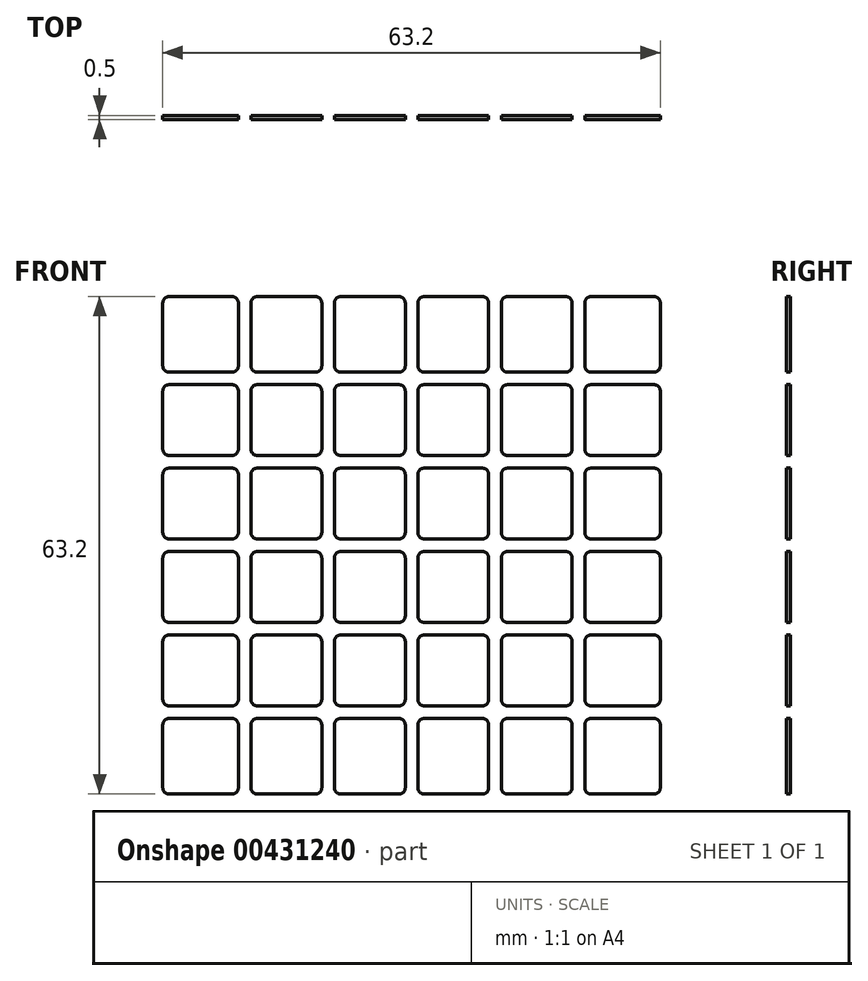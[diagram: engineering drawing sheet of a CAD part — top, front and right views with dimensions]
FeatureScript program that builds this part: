
annotation { "Feature Type Name" : "Feature", "Feature Type Description" : "" }
export const myFeature = defineFeature(function(context is Context, id is Id, definition is map)
    precondition{}
    {
        {
            var Q0;
            Q0=qCreatedBy(makeId("Front.planeOp"),FACE);
            var sketch = newSketch(context, id + "F0", { "sketchPlane" : qUnion([Q0])});
            skLineSegment(sketch, "E0.bottom", {"start": v(0.8, 0) * mm, "end": v(8.2, 0) * mm});
            skLineSegment(sketch, "E0.top", {"start": v(0.8, 9) * mm, "end": v(8.2, 9) * mm});
            skLineSegment(sketch, "E0.left", {"start": v(0, 0.8) * mm, "end": v(0, 8.2) * mm});
            skLineSegment(sketch, "E0.right", {"start": v(9, 0.8) * mm, "end": v(9, 8.2) * mm});
            skPoint(sketch, "E1.visualSharp", {"position": v(0, 9) * mm});
            skArc(sketch, "E1.filletArc", {"start": v(0.8, 9) * mm, "mid": v(0.23, 8.77) * mm, "end": v(0, 8.2) * mm});
            skPoint(sketch, "E2.visualSharp", {"position": v(9, 9) * mm});
            skArc(sketch, "E2.filletArc", {"start": v(9, 8.2) * mm, "mid": v(8.77, 8.77) * mm, "end": v(8.2, 9) * mm});
            skPoint(sketch, "E3.visualSharp", {"position": v(9, 0) * mm});
            skArc(sketch, "E3.filletArc", {"start": v(8.2, 0) * mm, "mid": v(8.77, 0.23) * mm, "end": v(9, 0.8) * mm});
            skPoint(sketch, "E4.visualSharp", {"position": v(0, 0) * mm});
            skArc(sketch, "E4.filletArc", {"start": v(0, 0.8) * mm, "mid": v(0.23, 0.23) * mm, "end": v(0.8, 0) * mm});
            skLineSegment(sketch, "E5.0.1.0", {"start": v(9, 11.4) * mm, "end": v(9, 18.8) * mm});
            skPoint(sketch, "E5.0.1.1", {"position": v(0, 10.6) * mm});
            skLineSegment(sketch, "E5.0.1.2", {"start": v(0, 11.4) * mm, "end": v(0, 18.8) * mm});
            skLineSegment(sketch, "E5.0.1.3", {"start": v(0.8, 10.6) * mm, "end": v(8.2, 10.6) * mm});
            skPoint(sketch, "E5.0.1.4", {"position": v(9, 10.6) * mm});
            skLineSegment(sketch, "E5.0.1.5", {"start": v(0.8, 19.6) * mm, "end": v(8.2, 19.6) * mm});
            skPoint(sketch, "E5.0.1.6", {"position": v(0, 19.6) * mm});
            skPoint(sketch, "E5.0.1.7", {"position": v(9, 19.6) * mm});
            skArc(sketch, "E5.0.1.8", {"start": v(8.2, 10.6) * mm, "mid": v(8.77, 10.83) * mm, "end": v(9, 11.4) * mm});
            skArc(sketch, "E5.0.1.9", {"start": v(0.8, 19.6) * mm, "mid": v(0.23, 19.37) * mm, "end": v(0, 18.8) * mm});
            skArc(sketch, "E5.0.1.10", {"start": v(0, 11.4) * mm, "mid": v(0.23, 10.83) * mm, "end": v(0.8, 10.6) * mm});
            skArc(sketch, "E5.0.1.11", {"start": v(9, 18.8) * mm, "mid": v(8.77, 19.37) * mm, "end": v(8.2, 19.6) * mm});
            skLineSegment(sketch, "E5.0.2.0", {"start": v(9, 22) * mm, "end": v(9, 29.4) * mm});
            skPoint(sketch, "E5.0.2.1", {"position": v(0, 21.2) * mm});
            skLineSegment(sketch, "E5.0.2.2", {"start": v(0, 22) * mm, "end": v(0, 29.4) * mm});
            skLineSegment(sketch, "E5.0.2.3", {"start": v(0.8, 21.2) * mm, "end": v(8.2, 21.2) * mm});
            skPoint(sketch, "E5.0.2.4", {"position": v(9, 21.2) * mm});
            skLineSegment(sketch, "E5.0.2.5", {"start": v(0.8, 30.2) * mm, "end": v(8.2, 30.2) * mm});
            skPoint(sketch, "E5.0.2.6", {"position": v(0, 30.2) * mm});
            skPoint(sketch, "E5.0.2.7", {"position": v(9, 30.2) * mm});
            skArc(sketch, "E5.0.2.8", {"start": v(8.2, 21.2) * mm, "mid": v(8.77, 21.43) * mm, "end": v(9, 22) * mm});
            skArc(sketch, "E5.0.2.9", {"start": v(0.8, 30.2) * mm, "mid": v(0.23, 29.97) * mm, "end": v(0, 29.4) * mm});
            skArc(sketch, "E5.0.2.10", {"start": v(0, 22) * mm, "mid": v(0.23, 21.43) * mm, "end": v(0.8, 21.2) * mm});
            skArc(sketch, "E5.0.2.11", {"start": v(9, 29.4) * mm, "mid": v(8.77, 29.97) * mm, "end": v(8.2, 30.2) * mm});
            skLineSegment(sketch, "E5.0.3.0", {"start": v(9, 32.6) * mm, "end": v(9, 40) * mm});
            skPoint(sketch, "E5.0.3.1", {"position": v(0, 31.8) * mm});
            skLineSegment(sketch, "E5.0.3.2", {"start": v(0, 32.6) * mm, "end": v(0, 40) * mm});
            skLineSegment(sketch, "E5.0.3.3", {"start": v(0.8, 31.8) * mm, "end": v(8.2, 31.8) * mm});
            skPoint(sketch, "E5.0.3.4", {"position": v(9, 31.8) * mm});
            skLineSegment(sketch, "E5.0.3.5", {"start": v(0.8, 40.8) * mm, "end": v(8.2, 40.8) * mm});
            skPoint(sketch, "E5.0.3.6", {"position": v(0, 40.8) * mm});
            skPoint(sketch, "E5.0.3.7", {"position": v(9, 40.8) * mm});
            skArc(sketch, "E5.0.3.8", {"start": v(8.2, 31.8) * mm, "mid": v(8.77, 32.03) * mm, "end": v(9, 32.6) * mm});
            skArc(sketch, "E5.0.3.9", {"start": v(0.8, 40.8) * mm, "mid": v(0.23, 40.57) * mm, "end": v(0, 40) * mm});
            skArc(sketch, "E5.0.3.10", {"start": v(0, 32.6) * mm, "mid": v(0.23, 32.03) * mm, "end": v(0.8, 31.8) * mm});
            skArc(sketch, "E5.0.3.11", {"start": v(9, 40) * mm, "mid": v(8.77, 40.57) * mm, "end": v(8.2, 40.8) * mm});
            skLineSegment(sketch, "E5.1.0.0", {"start": v(19.6, 0.8) * mm, "end": v(19.6, 8.2) * mm});
            skPoint(sketch, "E5.1.0.1", {"position": v(10.6, 0) * mm});
            skLineSegment(sketch, "E5.1.0.2", {"start": v(10.6, 0.8) * mm, "end": v(10.6, 8.2) * mm});
            skLineSegment(sketch, "E5.1.0.3", {"start": v(11.4, 0) * mm, "end": v(18.8, 0) * mm});
            skPoint(sketch, "E5.1.0.4", {"position": v(19.6, 0) * mm});
            skLineSegment(sketch, "E5.1.0.5", {"start": v(11.4, 9) * mm, "end": v(18.8, 9) * mm});
            skPoint(sketch, "E5.1.0.6", {"position": v(10.6, 9) * mm});
            skPoint(sketch, "E5.1.0.7", {"position": v(19.6, 9) * mm});
            skArc(sketch, "E5.1.0.8", {"start": v(18.8, 0) * mm, "mid": v(19.37, 0.23) * mm, "end": v(19.6, 0.8) * mm});
            skArc(sketch, "E5.1.0.9", {"start": v(11.4, 9) * mm, "mid": v(10.83, 8.77) * mm, "end": v(10.6, 8.2) * mm});
            skArc(sketch, "E5.1.0.10", {"start": v(10.6, 0.8) * mm, "mid": v(10.83, 0.23) * mm, "end": v(11.4, 0) * mm});
            skArc(sketch, "E5.1.0.11", {"start": v(19.6, 8.2) * mm, "mid": v(19.37, 8.77) * mm, "end": v(18.8, 9) * mm});
            skLineSegment(sketch, "E5.1.1.0", {"start": v(19.6, 11.4) * mm, "end": v(19.6, 18.8) * mm});
            skPoint(sketch, "E5.1.1.1", {"position": v(10.6, 10.6) * mm});
            skLineSegment(sketch, "E5.1.1.2", {"start": v(10.6, 11.4) * mm, "end": v(10.6, 18.8) * mm});
            skLineSegment(sketch, "E5.1.1.3", {"start": v(11.4, 10.6) * mm, "end": v(18.8, 10.6) * mm});
            skPoint(sketch, "E5.1.1.4", {"position": v(19.6, 10.6) * mm});
            skLineSegment(sketch, "E5.1.1.5", {"start": v(11.4, 19.6) * mm, "end": v(18.8, 19.6) * mm});
            skPoint(sketch, "E5.1.1.6", {"position": v(10.6, 19.6) * mm});
            skPoint(sketch, "E5.1.1.7", {"position": v(19.6, 19.6) * mm});
            skArc(sketch, "E5.1.1.8", {"start": v(18.8, 10.6) * mm, "mid": v(19.37, 10.83) * mm, "end": v(19.6, 11.4) * mm});
            skArc(sketch, "E5.1.1.9", {"start": v(11.4, 19.6) * mm, "mid": v(10.83, 19.37) * mm, "end": v(10.6, 18.8) * mm});
            skArc(sketch, "E5.1.1.10", {"start": v(10.6, 11.4) * mm, "mid": v(10.83, 10.83) * mm, "end": v(11.4, 10.6) * mm});
            skArc(sketch, "E5.1.1.11", {"start": v(19.6, 18.8) * mm, "mid": v(19.37, 19.37) * mm, "end": v(18.8, 19.6) * mm});
            skLineSegment(sketch, "E5.1.2.0", {"start": v(19.6, 22) * mm, "end": v(19.6, 29.4) * mm});
            skPoint(sketch, "E5.1.2.1", {"position": v(10.6, 21.2) * mm});
            skLineSegment(sketch, "E5.1.2.2", {"start": v(10.6, 22) * mm, "end": v(10.6, 29.4) * mm});
            skLineSegment(sketch, "E5.1.2.3", {"start": v(11.4, 21.2) * mm, "end": v(18.8, 21.2) * mm});
            skPoint(sketch, "E5.1.2.4", {"position": v(19.6, 21.2) * mm});
            skLineSegment(sketch, "E5.1.2.5", {"start": v(11.4, 30.2) * mm, "end": v(18.8, 30.2) * mm});
            skPoint(sketch, "E5.1.2.6", {"position": v(10.6, 30.2) * mm});
            skPoint(sketch, "E5.1.2.7", {"position": v(19.6, 30.2) * mm});
            skArc(sketch, "E5.1.2.8", {"start": v(18.8, 21.2) * mm, "mid": v(19.37, 21.43) * mm, "end": v(19.6, 22) * mm});
            skArc(sketch, "E5.1.2.9", {"start": v(11.4, 30.2) * mm, "mid": v(10.83, 29.97) * mm, "end": v(10.6, 29.4) * mm});
            skArc(sketch, "E5.1.2.10", {"start": v(10.6, 22) * mm, "mid": v(10.83, 21.43) * mm, "end": v(11.4, 21.2) * mm});
            skArc(sketch, "E5.1.2.11", {"start": v(19.6, 29.4) * mm, "mid": v(19.37, 29.97) * mm, "end": v(18.8, 30.2) * mm});
            skLineSegment(sketch, "E5.1.3.0", {"start": v(19.6, 32.6) * mm, "end": v(19.6, 40) * mm});
            skPoint(sketch, "E5.1.3.1", {"position": v(10.6, 31.8) * mm});
            skLineSegment(sketch, "E5.1.3.2", {"start": v(10.6, 32.6) * mm, "end": v(10.6, 40) * mm});
            skLineSegment(sketch, "E5.1.3.3", {"start": v(11.4, 31.8) * mm, "end": v(18.8, 31.8) * mm});
            skPoint(sketch, "E5.1.3.4", {"position": v(19.6, 31.8) * mm});
            skLineSegment(sketch, "E5.1.3.5", {"start": v(11.4, 40.8) * mm, "end": v(18.8, 40.8) * mm});
            skPoint(sketch, "E5.1.3.6", {"position": v(10.6, 40.8) * mm});
            skPoint(sketch, "E5.1.3.7", {"position": v(19.6, 40.8) * mm});
            skArc(sketch, "E5.1.3.8", {"start": v(18.8, 31.8) * mm, "mid": v(19.37, 32.03) * mm, "end": v(19.6, 32.6) * mm});
            skArc(sketch, "E5.1.3.9", {"start": v(11.4, 40.8) * mm, "mid": v(10.83, 40.57) * mm, "end": v(10.6, 40) * mm});
            skArc(sketch, "E5.1.3.10", {"start": v(10.6, 32.6) * mm, "mid": v(10.83, 32.03) * mm, "end": v(11.4, 31.8) * mm});
            skArc(sketch, "E5.1.3.11", {"start": v(19.6, 40) * mm, "mid": v(19.37, 40.57) * mm, "end": v(18.8, 40.8) * mm});
            skLineSegment(sketch, "E5.2.0.0", {"start": v(30.2, 0.8) * mm, "end": v(30.2, 8.2) * mm});
            skPoint(sketch, "E5.2.0.1", {"position": v(21.2, 0) * mm});
            skLineSegment(sketch, "E5.2.0.2", {"start": v(21.2, 0.8) * mm, "end": v(21.2, 8.2) * mm});
            skLineSegment(sketch, "E5.2.0.3", {"start": v(22, 0) * mm, "end": v(29.4, 0) * mm});
            skPoint(sketch, "E5.2.0.4", {"position": v(30.2, 0) * mm});
            skLineSegment(sketch, "E5.2.0.5", {"start": v(22, 9) * mm, "end": v(29.4, 9) * mm});
            skPoint(sketch, "E5.2.0.6", {"position": v(21.2, 9) * mm});
            skPoint(sketch, "E5.2.0.7", {"position": v(30.2, 9) * mm});
            skArc(sketch, "E5.2.0.8", {"start": v(29.4, 0) * mm, "mid": v(29.97, 0.23) * mm, "end": v(30.2, 0.8) * mm});
            skArc(sketch, "E5.2.0.9", {"start": v(22, 9) * mm, "mid": v(21.43, 8.77) * mm, "end": v(21.2, 8.2) * mm});
            skArc(sketch, "E5.2.0.10", {"start": v(21.2, 0.8) * mm, "mid": v(21.43, 0.23) * mm, "end": v(22, 0) * mm});
            skArc(sketch, "E5.2.0.11", {"start": v(30.2, 8.2) * mm, "mid": v(29.97, 8.77) * mm, "end": v(29.4, 9) * mm});
            skLineSegment(sketch, "E5.2.1.0", {"start": v(30.2, 11.4) * mm, "end": v(30.2, 18.8) * mm});
            skPoint(sketch, "E5.2.1.1", {"position": v(21.2, 10.6) * mm});
            skLineSegment(sketch, "E5.2.1.2", {"start": v(21.2, 11.4) * mm, "end": v(21.2, 18.8) * mm});
            skLineSegment(sketch, "E5.2.1.3", {"start": v(22, 10.6) * mm, "end": v(29.4, 10.6) * mm});
            skPoint(sketch, "E5.2.1.4", {"position": v(30.2, 10.6) * mm});
            skLineSegment(sketch, "E5.2.1.5", {"start": v(22, 19.6) * mm, "end": v(29.4, 19.6) * mm});
            skPoint(sketch, "E5.2.1.6", {"position": v(21.2, 19.6) * mm});
            skPoint(sketch, "E5.2.1.7", {"position": v(30.2, 19.6) * mm});
            skArc(sketch, "E5.2.1.8", {"start": v(29.4, 10.6) * mm, "mid": v(29.97, 10.83) * mm, "end": v(30.2, 11.4) * mm});
            skArc(sketch, "E5.2.1.9", {"start": v(22, 19.6) * mm, "mid": v(21.43, 19.37) * mm, "end": v(21.2, 18.8) * mm});
            skArc(sketch, "E5.2.1.10", {"start": v(21.2, 11.4) * mm, "mid": v(21.43, 10.83) * mm, "end": v(22, 10.6) * mm});
            skArc(sketch, "E5.2.1.11", {"start": v(30.2, 18.8) * mm, "mid": v(29.97, 19.37) * mm, "end": v(29.4, 19.6) * mm});
            skLineSegment(sketch, "E5.2.2.0", {"start": v(30.2, 22) * mm, "end": v(30.2, 29.4) * mm});
            skPoint(sketch, "E5.2.2.1", {"position": v(21.2, 21.2) * mm});
            skLineSegment(sketch, "E5.2.2.2", {"start": v(21.2, 22) * mm, "end": v(21.2, 29.4) * mm});
            skLineSegment(sketch, "E5.2.2.3", {"start": v(22, 21.2) * mm, "end": v(29.4, 21.2) * mm});
            skPoint(sketch, "E5.2.2.4", {"position": v(30.2, 21.2) * mm});
            skLineSegment(sketch, "E5.2.2.5", {"start": v(22, 30.2) * mm, "end": v(29.4, 30.2) * mm});
            skPoint(sketch, "E5.2.2.6", {"position": v(21.2, 30.2) * mm});
            skPoint(sketch, "E5.2.2.7", {"position": v(30.2, 30.2) * mm});
            skArc(sketch, "E5.2.2.8", {"start": v(29.4, 21.2) * mm, "mid": v(29.97, 21.43) * mm, "end": v(30.2, 22) * mm});
            skArc(sketch, "E5.2.2.9", {"start": v(22, 30.2) * mm, "mid": v(21.43, 29.97) * mm, "end": v(21.2, 29.4) * mm});
            skArc(sketch, "E5.2.2.10", {"start": v(21.2, 22) * mm, "mid": v(21.43, 21.43) * mm, "end": v(22, 21.2) * mm});
            skArc(sketch, "E5.2.2.11", {"start": v(30.2, 29.4) * mm, "mid": v(29.97, 29.97) * mm, "end": v(29.4, 30.2) * mm});
            skLineSegment(sketch, "E5.2.3.0", {"start": v(30.2, 32.6) * mm, "end": v(30.2, 40) * mm});
            skPoint(sketch, "E5.2.3.1", {"position": v(21.2, 31.8) * mm});
            skLineSegment(sketch, "E5.2.3.2", {"start": v(21.2, 32.6) * mm, "end": v(21.2, 40) * mm});
            skLineSegment(sketch, "E5.2.3.3", {"start": v(22, 31.8) * mm, "end": v(29.4, 31.8) * mm});
            skPoint(sketch, "E5.2.3.4", {"position": v(30.2, 31.8) * mm});
            skLineSegment(sketch, "E5.2.3.5", {"start": v(22, 40.8) * mm, "end": v(29.4, 40.8) * mm});
            skPoint(sketch, "E5.2.3.6", {"position": v(21.2, 40.8) * mm});
            skPoint(sketch, "E5.2.3.7", {"position": v(30.2, 40.8) * mm});
            skArc(sketch, "E5.2.3.8", {"start": v(29.4, 31.8) * mm, "mid": v(29.97, 32.03) * mm, "end": v(30.2, 32.6) * mm});
            skArc(sketch, "E5.2.3.9", {"start": v(22, 40.8) * mm, "mid": v(21.43, 40.57) * mm, "end": v(21.2, 40) * mm});
            skArc(sketch, "E5.2.3.10", {"start": v(21.2, 32.6) * mm, "mid": v(21.43, 32.03) * mm, "end": v(22, 31.8) * mm});
            skArc(sketch, "E5.2.3.11", {"start": v(30.2, 40) * mm, "mid": v(29.97, 40.57) * mm, "end": v(29.4, 40.8) * mm});
            skLineSegment(sketch, "E5.3.0.0", {"start": v(40.8, 0.8) * mm, "end": v(40.8, 8.2) * mm});
            skPoint(sketch, "E5.3.0.1", {"position": v(31.8, 0) * mm});
            skLineSegment(sketch, "E5.3.0.2", {"start": v(31.8, 0.8) * mm, "end": v(31.8, 8.2) * mm});
            skLineSegment(sketch, "E5.3.0.3", {"start": v(32.6, 0) * mm, "end": v(40, 0) * mm});
            skPoint(sketch, "E5.3.0.4", {"position": v(40.8, 0) * mm});
            skLineSegment(sketch, "E5.3.0.5", {"start": v(32.6, 9) * mm, "end": v(40, 9) * mm});
            skPoint(sketch, "E5.3.0.6", {"position": v(31.8, 9) * mm});
            skPoint(sketch, "E5.3.0.7", {"position": v(40.8, 9) * mm});
            skArc(sketch, "E5.3.0.8", {"start": v(40, 0) * mm, "mid": v(40.57, 0.23) * mm, "end": v(40.8, 0.8) * mm});
            skArc(sketch, "E5.3.0.9", {"start": v(32.6, 9) * mm, "mid": v(32.03, 8.77) * mm, "end": v(31.8, 8.2) * mm});
            skArc(sketch, "E5.3.0.10", {"start": v(31.8, 0.8) * mm, "mid": v(32.03, 0.23) * mm, "end": v(32.6, 0) * mm});
            skArc(sketch, "E5.3.0.11", {"start": v(40.8, 8.2) * mm, "mid": v(40.57, 8.77) * mm, "end": v(40, 9) * mm});
            skLineSegment(sketch, "E5.3.1.0", {"start": v(40.8, 11.4) * mm, "end": v(40.8, 18.8) * mm});
            skPoint(sketch, "E5.3.1.1", {"position": v(31.8, 10.6) * mm});
            skLineSegment(sketch, "E5.3.1.2", {"start": v(31.8, 11.4) * mm, "end": v(31.8, 18.8) * mm});
            skLineSegment(sketch, "E5.3.1.3", {"start": v(32.6, 10.6) * mm, "end": v(40, 10.6) * mm});
            skPoint(sketch, "E5.3.1.4", {"position": v(40.8, 10.6) * mm});
            skLineSegment(sketch, "E5.3.1.5", {"start": v(32.6, 19.6) * mm, "end": v(40, 19.6) * mm});
            skPoint(sketch, "E5.3.1.6", {"position": v(31.8, 19.6) * mm});
            skPoint(sketch, "E5.3.1.7", {"position": v(40.8, 19.6) * mm});
            skArc(sketch, "E5.3.1.8", {"start": v(40, 10.6) * mm, "mid": v(40.57, 10.83) * mm, "end": v(40.8, 11.4) * mm});
            skArc(sketch, "E5.3.1.9", {"start": v(32.6, 19.6) * mm, "mid": v(32.03, 19.37) * mm, "end": v(31.8, 18.8) * mm});
            skArc(sketch, "E5.3.1.10", {"start": v(31.8, 11.4) * mm, "mid": v(32.03, 10.83) * mm, "end": v(32.6, 10.6) * mm});
            skArc(sketch, "E5.3.1.11", {"start": v(40.8, 18.8) * mm, "mid": v(40.57, 19.37) * mm, "end": v(40, 19.6) * mm});
            skLineSegment(sketch, "E5.3.2.0", {"start": v(40.8, 22) * mm, "end": v(40.8, 29.4) * mm});
            skPoint(sketch, "E5.3.2.1", {"position": v(31.8, 21.2) * mm});
            skLineSegment(sketch, "E5.3.2.2", {"start": v(31.8, 22) * mm, "end": v(31.8, 29.4) * mm});
            skLineSegment(sketch, "E5.3.2.3", {"start": v(32.6, 21.2) * mm, "end": v(40, 21.2) * mm});
            skPoint(sketch, "E5.3.2.4", {"position": v(40.8, 21.2) * mm});
            skLineSegment(sketch, "E5.3.2.5", {"start": v(32.6, 30.2) * mm, "end": v(40, 30.2) * mm});
            skPoint(sketch, "E5.3.2.6", {"position": v(31.8, 30.2) * mm});
            skPoint(sketch, "E5.3.2.7", {"position": v(40.8, 30.2) * mm});
            skArc(sketch, "E5.3.2.8", {"start": v(40, 21.2) * mm, "mid": v(40.57, 21.43) * mm, "end": v(40.8, 22) * mm});
            skArc(sketch, "E5.3.2.9", {"start": v(32.6, 30.2) * mm, "mid": v(32.03, 29.97) * mm, "end": v(31.8, 29.4) * mm});
            skArc(sketch, "E5.3.2.10", {"start": v(31.8, 22) * mm, "mid": v(32.03, 21.43) * mm, "end": v(32.6, 21.2) * mm});
            skArc(sketch, "E5.3.2.11", {"start": v(40.8, 29.4) * mm, "mid": v(40.57, 29.97) * mm, "end": v(40, 30.2) * mm});
            skLineSegment(sketch, "E5.3.3.0", {"start": v(40.8, 32.6) * mm, "end": v(40.8, 40) * mm});
            skPoint(sketch, "E5.3.3.1", {"position": v(31.8, 31.8) * mm});
            skLineSegment(sketch, "E5.3.3.2", {"start": v(31.8, 32.6) * mm, "end": v(31.8, 40) * mm});
            skLineSegment(sketch, "E5.3.3.3", {"start": v(32.6, 31.8) * mm, "end": v(40, 31.8) * mm});
            skPoint(sketch, "E5.3.3.4", {"position": v(40.8, 31.8) * mm});
            skLineSegment(sketch, "E5.3.3.5", {"start": v(32.6, 40.8) * mm, "end": v(40, 40.8) * mm});
            skPoint(sketch, "E5.3.3.6", {"position": v(31.8, 40.8) * mm});
            skPoint(sketch, "E5.3.3.7", {"position": v(40.8, 40.8) * mm});
            skArc(sketch, "E5.3.3.8", {"start": v(40, 31.8) * mm, "mid": v(40.57, 32.03) * mm, "end": v(40.8, 32.6) * mm});
            skArc(sketch, "E5.3.3.9", {"start": v(32.6, 40.8) * mm, "mid": v(32.03, 40.57) * mm, "end": v(31.8, 40) * mm});
            skArc(sketch, "E5.3.3.10", {"start": v(31.8, 32.6) * mm, "mid": v(32.03, 32.03) * mm, "end": v(32.6, 31.8) * mm});
            skArc(sketch, "E5.3.3.11", {"start": v(40.8, 40) * mm, "mid": v(40.57, 40.57) * mm, "end": v(40, 40.8) * mm});
            skLineSegment(sketch, "E5.direction1", {"start": v(0, 0) * mm, "end": v(10.6, 0) * mm, "construction": true});
            skLineSegment(sketch, "E5.direction2", {"start": v(0, 0) * mm, "end": v(0, 10.6) * mm, "construction": true});
            skLineSegment(sketch, "E6.bottom", {"start": v(-2.4, 0) * mm, "end": v(-10.4, 0) * mm});
            skLineSegment(sketch, "E6.top", {"start": v(-2.4, 9) * mm, "end": v(-10.4, 9) * mm});
            skLineSegment(sketch, "E6.left", {"start": v(-1.6, 0.8) * mm, "end": v(-1.6, 8.2) * mm});
            skLineSegment(sketch, "E6.right", {"start": v(-11.2, 0.8) * mm, "end": v(-11.2, 8.2) * mm});
            skPoint(sketch, "E7.visualSharp", {"position": v(-11.2, 9) * mm});
            skArc(sketch, "E7.filletArc", {"start": v(-10.4, 9) * mm, "mid": v(-10.97, 8.77) * mm, "end": v(-11.2, 8.2) * mm});
            skPoint(sketch, "E8.visualSharp", {"position": v(-1.6, 9) * mm});
            skArc(sketch, "E8.filletArc", {"start": v(-1.6, 8.2) * mm, "mid": v(-1.83, 8.77) * mm, "end": v(-2.4, 9) * mm});
            skPoint(sketch, "E9.visualSharp", {"position": v(-1.6, 0) * mm});
            skArc(sketch, "E9.filletArc", {"start": v(-2.4, 0) * mm, "mid": v(-1.83, 0.23) * mm, "end": v(-1.6, 0.8) * mm});
            skPoint(sketch, "E10.visualSharp", {"position": v(-11.2, 0) * mm});
            skArc(sketch, "E10.filletArc", {"start": v(-11.2, 0.8) * mm, "mid": v(-10.97, 0.23) * mm, "end": v(-10.4, 0) * mm});
            skPoint(sketch, "E11.0.1.0", {"position": v(-1.6, 10.6) * mm});
            skLineSegment(sketch, "E11.0.1.1", {"start": v(-2.4, 10.6) * mm, "end": v(-10.4, 10.6) * mm});
            skLineSegment(sketch, "E11.0.1.2", {"start": v(-1.6, 11.4) * mm, "end": v(-1.6, 18.8) * mm});
            skLineSegment(sketch, "E11.0.1.3", {"start": v(-2.4, 19.6) * mm, "end": v(-10.4, 19.6) * mm});
            skPoint(sketch, "E11.0.1.4", {"position": v(-11.2, 19.6) * mm});
            skPoint(sketch, "E11.0.1.5", {"position": v(-11.2, 10.6) * mm});
            skPoint(sketch, "E11.0.1.6", {"position": v(-1.6, 19.6) * mm});
            skLineSegment(sketch, "E11.0.1.7", {"start": v(-11.2, 11.4) * mm, "end": v(-11.2, 18.8) * mm});
            skArc(sketch, "E11.0.1.8", {"start": v(-10.4, 19.6) * mm, "mid": v(-10.97, 19.37) * mm, "end": v(-11.2, 18.8) * mm});
            skArc(sketch, "E11.0.1.9", {"start": v(-2.4, 10.6) * mm, "mid": v(-1.83, 10.83) * mm, "end": v(-1.6, 11.4) * mm});
            skArc(sketch, "E11.0.1.10", {"start": v(-1.6, 18.8) * mm, "mid": v(-1.83, 19.37) * mm, "end": v(-2.4, 19.6) * mm});
            skArc(sketch, "E11.0.1.11", {"start": v(-11.2, 11.4) * mm, "mid": v(-10.97, 10.83) * mm, "end": v(-10.4, 10.6) * mm});
            skPoint(sketch, "E11.0.2.0", {"position": v(-1.6, 21.2) * mm});
            skLineSegment(sketch, "E11.0.2.1", {"start": v(-2.4, 21.2) * mm, "end": v(-10.4, 21.2) * mm});
            skLineSegment(sketch, "E11.0.2.2", {"start": v(-1.6, 22) * mm, "end": v(-1.6, 29.4) * mm});
            skLineSegment(sketch, "E11.0.2.3", {"start": v(-2.4, 30.2) * mm, "end": v(-10.4, 30.2) * mm});
            skPoint(sketch, "E11.0.2.4", {"position": v(-11.2, 30.2) * mm});
            skPoint(sketch, "E11.0.2.5", {"position": v(-11.2, 21.2) * mm});
            skPoint(sketch, "E11.0.2.6", {"position": v(-1.6, 30.2) * mm});
            skLineSegment(sketch, "E11.0.2.7", {"start": v(-11.2, 22) * mm, "end": v(-11.2, 29.4) * mm});
            skArc(sketch, "E11.0.2.8", {"start": v(-10.4, 30.2) * mm, "mid": v(-10.97, 29.97) * mm, "end": v(-11.2, 29.4) * mm});
            skArc(sketch, "E11.0.2.9", {"start": v(-2.4, 21.2) * mm, "mid": v(-1.83, 21.43) * mm, "end": v(-1.6, 22) * mm});
            skArc(sketch, "E11.0.2.10", {"start": v(-1.6, 29.4) * mm, "mid": v(-1.83, 29.97) * mm, "end": v(-2.4, 30.2) * mm});
            skArc(sketch, "E11.0.2.11", {"start": v(-11.2, 22) * mm, "mid": v(-10.97, 21.43) * mm, "end": v(-10.4, 21.2) * mm});
            skPoint(sketch, "E11.0.3.0", {"position": v(-1.6, 31.8) * mm});
            skLineSegment(sketch, "E11.0.3.1", {"start": v(-2.4, 31.8) * mm, "end": v(-10.4, 31.8) * mm});
            skLineSegment(sketch, "E11.0.3.2", {"start": v(-1.6, 32.6) * mm, "end": v(-1.6, 40) * mm});
            skLineSegment(sketch, "E11.0.3.3", {"start": v(-2.4, 40.8) * mm, "end": v(-10.4, 40.8) * mm});
            skPoint(sketch, "E11.0.3.4", {"position": v(-11.2, 40.8) * mm});
            skPoint(sketch, "E11.0.3.5", {"position": v(-11.2, 31.8) * mm});
            skPoint(sketch, "E11.0.3.6", {"position": v(-1.6, 40.8) * mm});
            skLineSegment(sketch, "E11.0.3.7", {"start": v(-11.2, 32.6) * mm, "end": v(-11.2, 40) * mm});
            skArc(sketch, "E11.0.3.8", {"start": v(-10.4, 40.8) * mm, "mid": v(-10.97, 40.57) * mm, "end": v(-11.2, 40) * mm});
            skArc(sketch, "E11.0.3.9", {"start": v(-2.4, 31.8) * mm, "mid": v(-1.83, 32.03) * mm, "end": v(-1.6, 32.6) * mm});
            skArc(sketch, "E11.0.3.10", {"start": v(-1.6, 40) * mm, "mid": v(-1.83, 40.57) * mm, "end": v(-2.4, 40.8) * mm});
            skArc(sketch, "E11.0.3.11", {"start": v(-11.2, 32.6) * mm, "mid": v(-10.97, 32.03) * mm, "end": v(-10.4, 31.8) * mm});
            skLineSegment(sketch, "E11.direction1", {"start": v(-11.2, 0) * mm, "end": v(16.8, 0) * mm, "construction": true});
            skLineSegment(sketch, "E11.direction2", {"start": v(-11.2, 0) * mm, "end": v(-11.2, 10.6) * mm, "construction": true});
            skLineSegment(sketch, "E12.bottom", {"start": v(-2.4, 42.4) * mm, "end": v(-10.4, 42.4) * mm});
            skLineSegment(sketch, "E12.top", {"start": v(-2.4, 52) * mm, "end": v(-10.4, 52) * mm});
            skLineSegment(sketch, "E12.left", {"start": v(-1.6, 43.2) * mm, "end": v(-1.6, 51.2) * mm});
            skLineSegment(sketch, "E12.right", {"start": v(-11.2, 43.2) * mm, "end": v(-11.2, 51.2) * mm});
            skPoint(sketch, "E13.visualSharp", {"position": v(-11.2, 42.4) * mm});
            skArc(sketch, "E13.filletArc", {"start": v(-11.2, 43.2) * mm, "mid": v(-10.97, 42.63) * mm, "end": v(-10.4, 42.4) * mm});
            skPoint(sketch, "E14.visualSharp", {"position": v(-1.6, 42.4) * mm});
            skArc(sketch, "E14.filletArc", {"start": v(-2.4, 42.4) * mm, "mid": v(-1.83, 42.63) * mm, "end": v(-1.6, 43.2) * mm});
            skPoint(sketch, "E15.visualSharp", {"position": v(-1.6, 52) * mm});
            skArc(sketch, "E15.filletArc", {"start": v(-1.6, 51.2) * mm, "mid": v(-1.83, 51.77) * mm, "end": v(-2.4, 52) * mm});
            skPoint(sketch, "E16.visualSharp", {"position": v(-11.2, 52) * mm});
            skArc(sketch, "E16.filletArc", {"start": v(-10.4, 52) * mm, "mid": v(-10.97, 51.77) * mm, "end": v(-11.2, 51.2) * mm});
            skLineSegment(sketch, "E17", {"start": v(19.6, 21.2) * mm, "end": v(21.2, 19.6) * mm, "construction": true});
            skLineSegment(sketch, "E18.1.0", {"start": v(18.8, -11.2) * mm, "end": v(11.4, -11.2) * mm});
            skPoint(sketch, "E18.1.1", {"position": v(0, -1.6) * mm});
            skPoint(sketch, "E18.1.2", {"position": v(21.2, -1.6) * mm});
            skLineSegment(sketch, "E18.1.3", {"start": v(8.2, -11.2) * mm, "end": v(0.8, -11.2) * mm});
            skLineSegment(sketch, "E18.1.4", {"start": v(21.2, -2.4) * mm, "end": v(21.2, -10.4) * mm});
            skPoint(sketch, "E18.1.5", {"position": v(30.2, -1.6) * mm});
            skPoint(sketch, "E18.1.6", {"position": v(-11.2, -1.6) * mm});
            skPoint(sketch, "E18.1.7", {"position": v(10.6, -1.6) * mm});
            skLineSegment(sketch, "E18.1.8", {"start": v(10.6, -2.4) * mm, "end": v(10.6, -10.4) * mm});
            skPoint(sketch, "E18.1.9", {"position": v(9, -1.6) * mm});
            skLineSegment(sketch, "E18.1.10", {"start": v(-1.6, -2.4) * mm, "end": v(-1.6, -10.4) * mm});
            skPoint(sketch, "E18.1.11", {"position": v(40.8, -1.6) * mm});
            skPoint(sketch, "E18.1.12", {"position": v(31.8, -1.6) * mm});
            skLineSegment(sketch, "E18.1.13", {"start": v(29.4, -1.6) * mm, "end": v(22, -1.6) * mm});
            skPoint(sketch, "E18.1.14", {"position": v(30.2, -11.2) * mm});
            skLineSegment(sketch, "E18.1.15", {"start": v(-11.2, -2.4) * mm, "end": v(-11.2, -10.4) * mm});
            skLineSegment(sketch, "E18.1.16", {"start": v(9, -2.4) * mm, "end": v(9, -10.4) * mm});
            skLineSegment(sketch, "E18.1.17", {"start": v(-2.4, -11.2) * mm, "end": v(-10.4, -11.2) * mm});
            skLineSegment(sketch, "E18.1.18", {"start": v(0, -2.4) * mm, "end": v(0, -10.4) * mm});
            skLineSegment(sketch, "E18.1.19", {"start": v(40.8, -11.2) * mm, "end": v(30.2, -11.2) * mm, "construction": true});
            skLineSegment(sketch, "E18.1.20", {"start": v(19.6, -2.4) * mm, "end": v(19.6, -10.4) * mm});
            skPoint(sketch, "E18.1.21", {"position": v(19.6, -11.2) * mm});
            skLineSegment(sketch, "E18.1.22", {"start": v(40.8, -2.4) * mm, "end": v(40.8, -10.4) * mm});
            skPoint(sketch, "E18.1.23", {"position": v(-1.6, -1.6) * mm});
            skPoint(sketch, "E18.1.24", {"position": v(31.8, -11.2) * mm});
            skPoint(sketch, "E18.1.25", {"position": v(9, -11.2) * mm});
            skLineSegment(sketch, "E18.1.26", {"start": v(40, -1.6) * mm, "end": v(32.6, -1.6) * mm});
            skLineSegment(sketch, "E18.1.27", {"start": v(18.8, -1.6) * mm, "end": v(11.4, -1.6) * mm});
            skLineSegment(sketch, "E18.1.28", {"start": v(8.2, -1.6) * mm, "end": v(0.8, -1.6) * mm});
            skLineSegment(sketch, "E18.1.29", {"start": v(29.4, -11.2) * mm, "end": v(22, -11.2) * mm});
            skLineSegment(sketch, "E18.1.30", {"start": v(30.2, -2.4) * mm, "end": v(30.2, -10.4) * mm});
            skPoint(sketch, "E18.1.31", {"position": v(-11.2, -11.2) * mm});
            skPoint(sketch, "E18.1.32", {"position": v(0, -11.2) * mm});
            skPoint(sketch, "E18.1.33", {"position": v(40.8, -11.2) * mm});
            skPoint(sketch, "E18.1.34", {"position": v(10.6, -11.2) * mm});
            skPoint(sketch, "E18.1.35", {"position": v(19.6, -1.6) * mm});
            skPoint(sketch, "E18.1.36", {"position": v(21.2, -11.2) * mm});
            skPoint(sketch, "E18.1.37", {"position": v(-1.6, -11.2) * mm});
            skLineSegment(sketch, "E18.1.38", {"start": v(31.8, -2.4) * mm, "end": v(31.8, -10.4) * mm});
            skLineSegment(sketch, "E18.1.39", {"start": v(-2.4, -1.6) * mm, "end": v(-10.4, -1.6) * mm});
            skLineSegment(sketch, "E18.1.40", {"start": v(40, -11.2) * mm, "end": v(32.6, -11.2) * mm});
            skArc(sketch, "E18.1.41", {"start": v(-2.4, -11.2) * mm, "mid": v(-1.83, -10.97) * mm, "end": v(-1.6, -10.4) * mm});
            skArc(sketch, "E18.1.42", {"start": v(21.2, -10.4) * mm, "mid": v(21.43, -10.97) * mm, "end": v(22, -11.2) * mm});
            skArc(sketch, "E18.1.43", {"start": v(22, -1.6) * mm, "mid": v(21.43, -1.83) * mm, "end": v(21.2, -2.4) * mm});
            skArc(sketch, "E18.1.44", {"start": v(31.8, -10.4) * mm, "mid": v(32.03, -10.97) * mm, "end": v(32.6, -11.2) * mm});
            skArc(sketch, "E18.1.45", {"start": v(32.6, -1.6) * mm, "mid": v(32.03, -1.83) * mm, "end": v(31.8, -2.4) * mm});
            skArc(sketch, "E18.1.46", {"start": v(30.2, -2.4) * mm, "mid": v(29.97, -1.83) * mm, "end": v(29.4, -1.6) * mm});
            skArc(sketch, "E18.1.47", {"start": v(-1.6, -2.4) * mm, "mid": v(-1.83, -1.83) * mm, "end": v(-2.4, -1.6) * mm});
            skArc(sketch, "E18.1.48", {"start": v(0, -10.4) * mm, "mid": v(0.23, -10.97) * mm, "end": v(0.8, -11.2) * mm});
            skArc(sketch, "E18.1.49", {"start": v(-11.2, -10.4) * mm, "mid": v(-10.97, -10.97) * mm, "end": v(-10.4, -11.2) * mm});
            skArc(sketch, "E18.1.50", {"start": v(19.6, -2.4) * mm, "mid": v(19.37, -1.83) * mm, "end": v(18.8, -1.6) * mm});
            skArc(sketch, "E18.1.51", {"start": v(10.6, -10.4) * mm, "mid": v(10.83, -10.97) * mm, "end": v(11.4, -11.2) * mm});
            skArc(sketch, "E18.1.52", {"start": v(40, -11.2) * mm, "mid": v(40.57, -10.97) * mm, "end": v(40.8, -10.4) * mm});
            skArc(sketch, "E18.1.53", {"start": v(29.4, -11.2) * mm, "mid": v(29.97, -10.97) * mm, "end": v(30.2, -10.4) * mm});
            skArc(sketch, "E18.1.54", {"start": v(11.4, -1.6) * mm, "mid": v(10.83, -1.83) * mm, "end": v(10.6, -2.4) * mm});
            skArc(sketch, "E18.1.55", {"start": v(40.8, -2.4) * mm, "mid": v(40.57, -1.83) * mm, "end": v(40, -1.6) * mm});
            skArc(sketch, "E18.1.56", {"start": v(8.2, -11.2) * mm, "mid": v(8.77, -10.97) * mm, "end": v(9, -10.4) * mm});
            skArc(sketch, "E18.1.57", {"start": v(18.8, -11.2) * mm, "mid": v(19.37, -10.97) * mm, "end": v(19.6, -10.4) * mm});
            skArc(sketch, "E18.1.58", {"start": v(-10.4, -1.6) * mm, "mid": v(-10.97, -1.83) * mm, "end": v(-11.2, -2.4) * mm});
            skArc(sketch, "E18.1.59", {"start": v(9, -2.4) * mm, "mid": v(8.77, -1.83) * mm, "end": v(8.2, -1.6) * mm});
            skArc(sketch, "E18.1.60", {"start": v(0.8, -1.6) * mm, "mid": v(0.23, -1.83) * mm, "end": v(0, -2.4) * mm});
            skLineSegment(sketch, "E18.2.0", {"start": v(52, 18.8) * mm, "end": v(52, 11.4) * mm});
            skPoint(sketch, "E18.2.1", {"position": v(42.4, 0) * mm});
            skPoint(sketch, "E18.2.2", {"position": v(42.4, 21.2) * mm});
            skLineSegment(sketch, "E18.2.3", {"start": v(52, 8.2) * mm, "end": v(52, 0.8) * mm});
            skLineSegment(sketch, "E18.2.4", {"start": v(43.2, 21.2) * mm, "end": v(51.2, 21.2) * mm});
            skPoint(sketch, "E18.2.5", {"position": v(42.4, 30.2) * mm});
            skPoint(sketch, "E18.2.6", {"position": v(42.4, -11.2) * mm});
            skPoint(sketch, "E18.2.7", {"position": v(42.4, 10.6) * mm});
            skLineSegment(sketch, "E18.2.8", {"start": v(43.2, 10.6) * mm, "end": v(51.2, 10.6) * mm});
            skPoint(sketch, "E18.2.9", {"position": v(42.4, 9) * mm});
            skLineSegment(sketch, "E18.2.10", {"start": v(43.2, -1.6) * mm, "end": v(51.2, -1.6) * mm});
            skPoint(sketch, "E18.2.11", {"position": v(42.4, 40.8) * mm});
            skPoint(sketch, "E18.2.12", {"position": v(42.4, 31.8) * mm});
            skLineSegment(sketch, "E18.2.13", {"start": v(42.4, 29.4) * mm, "end": v(42.4, 22) * mm});
            skPoint(sketch, "E18.2.14", {"position": v(52, 30.2) * mm});
            skLineSegment(sketch, "E18.2.15", {"start": v(43.2, -11.2) * mm, "end": v(51.2, -11.2) * mm});
            skLineSegment(sketch, "E18.2.16", {"start": v(43.2, 9) * mm, "end": v(51.2, 9) * mm});
            skLineSegment(sketch, "E18.2.17", {"start": v(52, -2.4) * mm, "end": v(52, -10.4) * mm});
            skLineSegment(sketch, "E18.2.18", {"start": v(43.2, 0) * mm, "end": v(51.2, 0) * mm});
            skLineSegment(sketch, "E18.2.19", {"start": v(52, 40.8) * mm, "end": v(52, 30.2) * mm, "construction": true});
            skLineSegment(sketch, "E18.2.20", {"start": v(43.2, 19.6) * mm, "end": v(51.2, 19.6) * mm});
            skPoint(sketch, "E18.2.21", {"position": v(52, 19.6) * mm});
            skLineSegment(sketch, "E18.2.22", {"start": v(43.2, 40.8) * mm, "end": v(51.2, 40.8) * mm});
            skPoint(sketch, "E18.2.23", {"position": v(42.4, -1.6) * mm});
            skPoint(sketch, "E18.2.24", {"position": v(52, 31.8) * mm});
            skPoint(sketch, "E18.2.25", {"position": v(52, 9) * mm});
            skLineSegment(sketch, "E18.2.26", {"start": v(42.4, 40) * mm, "end": v(42.4, 32.6) * mm});
            skLineSegment(sketch, "E18.2.27", {"start": v(42.4, 18.8) * mm, "end": v(42.4, 11.4) * mm});
            skLineSegment(sketch, "E18.2.28", {"start": v(42.4, 8.2) * mm, "end": v(42.4, 0.8) * mm});
            skLineSegment(sketch, "E18.2.29", {"start": v(52, 29.4) * mm, "end": v(52, 22) * mm});
            skLineSegment(sketch, "E18.2.30", {"start": v(43.2, 30.2) * mm, "end": v(51.2, 30.2) * mm});
            skPoint(sketch, "E18.2.31", {"position": v(52, -11.2) * mm});
            skPoint(sketch, "E18.2.32", {"position": v(52, 0) * mm});
            skPoint(sketch, "E18.2.33", {"position": v(52, 40.8) * mm});
            skPoint(sketch, "E18.2.34", {"position": v(52, 10.6) * mm});
            skPoint(sketch, "E18.2.35", {"position": v(42.4, 19.6) * mm});
            skPoint(sketch, "E18.2.36", {"position": v(52, 21.2) * mm});
            skPoint(sketch, "E18.2.37", {"position": v(52, -1.6) * mm});
            skLineSegment(sketch, "E18.2.38", {"start": v(43.2, 31.8) * mm, "end": v(51.2, 31.8) * mm});
            skLineSegment(sketch, "E18.2.39", {"start": v(42.4, -2.4) * mm, "end": v(42.4, -10.4) * mm});
            skLineSegment(sketch, "E18.2.40", {"start": v(52, 40) * mm, "end": v(52, 32.6) * mm});
            skArc(sketch, "E18.2.41", {"start": v(52, -2.4) * mm, "mid": v(51.77, -1.83) * mm, "end": v(51.2, -1.6) * mm});
            skArc(sketch, "E18.2.42", {"start": v(51.2, 21.2) * mm, "mid": v(51.77, 21.43) * mm, "end": v(52, 22) * mm});
            skArc(sketch, "E18.2.43", {"start": v(42.4, 22) * mm, "mid": v(42.63, 21.43) * mm, "end": v(43.2, 21.2) * mm});
            skArc(sketch, "E18.2.44", {"start": v(51.2, 31.8) * mm, "mid": v(51.77, 32.03) * mm, "end": v(52, 32.6) * mm});
            skArc(sketch, "E18.2.45", {"start": v(42.4, 32.6) * mm, "mid": v(42.63, 32.03) * mm, "end": v(43.2, 31.8) * mm});
            skArc(sketch, "E18.2.46", {"start": v(43.2, 30.2) * mm, "mid": v(42.63, 29.97) * mm, "end": v(42.4, 29.4) * mm});
            skArc(sketch, "E18.2.47", {"start": v(43.2, -1.6) * mm, "mid": v(42.63, -1.83) * mm, "end": v(42.4, -2.4) * mm});
            skArc(sketch, "E18.2.48", {"start": v(51.2, 0) * mm, "mid": v(51.77, 0.23) * mm, "end": v(52, 0.8) * mm});
            skArc(sketch, "E18.2.49", {"start": v(51.2, -11.2) * mm, "mid": v(51.77, -10.97) * mm, "end": v(52, -10.4) * mm});
            skArc(sketch, "E18.2.50", {"start": v(43.2, 19.6) * mm, "mid": v(42.63, 19.37) * mm, "end": v(42.4, 18.8) * mm});
            skArc(sketch, "E18.2.51", {"start": v(51.2, 10.6) * mm, "mid": v(51.77, 10.83) * mm, "end": v(52, 11.4) * mm});
            skArc(sketch, "E18.2.52", {"start": v(52, 40) * mm, "mid": v(51.77, 40.57) * mm, "end": v(51.2, 40.8) * mm});
            skArc(sketch, "E18.2.53", {"start": v(52, 29.4) * mm, "mid": v(51.77, 29.97) * mm, "end": v(51.2, 30.2) * mm});
            skArc(sketch, "E18.2.54", {"start": v(42.4, 11.4) * mm, "mid": v(42.63, 10.83) * mm, "end": v(43.2, 10.6) * mm});
            skArc(sketch, "E18.2.55", {"start": v(43.2, 40.8) * mm, "mid": v(42.63, 40.57) * mm, "end": v(42.4, 40) * mm});
            skArc(sketch, "E18.2.56", {"start": v(52, 8.2) * mm, "mid": v(51.77, 8.77) * mm, "end": v(51.2, 9) * mm});
            skArc(sketch, "E18.2.57", {"start": v(52, 18.8) * mm, "mid": v(51.77, 19.37) * mm, "end": v(51.2, 19.6) * mm});
            skArc(sketch, "E18.2.58", {"start": v(42.4, -10.4) * mm, "mid": v(42.63, -10.97) * mm, "end": v(43.2, -11.2) * mm});
            skArc(sketch, "E18.2.59", {"start": v(43.2, 9) * mm, "mid": v(42.63, 8.77) * mm, "end": v(42.4, 8.2) * mm});
            skArc(sketch, "E18.2.60", {"start": v(42.4, 0.8) * mm, "mid": v(42.63, 0.23) * mm, "end": v(43.2, 0) * mm});
            skLineSegment(sketch, "E18.3.0", {"start": v(22, 52) * mm, "end": v(29.4, 52) * mm});
            skPoint(sketch, "E18.3.1", {"position": v(40.8, 42.4) * mm});
            skPoint(sketch, "E18.3.2", {"position": v(19.6, 42.4) * mm});
            skLineSegment(sketch, "E18.3.3", {"start": v(32.6, 52) * mm, "end": v(40, 52) * mm});
            skLineSegment(sketch, "E18.3.4", {"start": v(19.6, 43.2) * mm, "end": v(19.6, 51.2) * mm});
            skPoint(sketch, "E18.3.5", {"position": v(10.6, 42.4) * mm});
            skPoint(sketch, "E18.3.6", {"position": v(52, 42.4) * mm});
            skPoint(sketch, "E18.3.7", {"position": v(30.2, 42.4) * mm});
            skLineSegment(sketch, "E18.3.8", {"start": v(30.2, 43.2) * mm, "end": v(30.2, 51.2) * mm});
            skPoint(sketch, "E18.3.9", {"position": v(31.8, 42.4) * mm});
            skLineSegment(sketch, "E18.3.10", {"start": v(42.4, 43.2) * mm, "end": v(42.4, 51.2) * mm});
            skPoint(sketch, "E18.3.11", {"position": v(0, 42.4) * mm});
            skPoint(sketch, "E18.3.12", {"position": v(9, 42.4) * mm});
            skLineSegment(sketch, "E18.3.13", {"start": v(11.4, 42.4) * mm, "end": v(18.8, 42.4) * mm});
            skPoint(sketch, "E18.3.14", {"position": v(10.6, 52) * mm});
            skLineSegment(sketch, "E18.3.15", {"start": v(52, 43.2) * mm, "end": v(52, 51.2) * mm});
            skLineSegment(sketch, "E18.3.16", {"start": v(31.8, 43.2) * mm, "end": v(31.8, 51.2) * mm});
            skLineSegment(sketch, "E18.3.17", {"start": v(43.2, 52) * mm, "end": v(51.2, 52) * mm});
            skLineSegment(sketch, "E18.3.18", {"start": v(40.8, 43.2) * mm, "end": v(40.8, 51.2) * mm});
            skLineSegment(sketch, "E18.3.19", {"start": v(0, 52) * mm, "end": v(10.6, 52) * mm, "construction": true});
            skLineSegment(sketch, "E18.3.20", {"start": v(21.2, 43.2) * mm, "end": v(21.2, 51.2) * mm});
            skPoint(sketch, "E18.3.21", {"position": v(21.2, 52) * mm});
            skLineSegment(sketch, "E18.3.22", {"start": v(0, 43.2) * mm, "end": v(0, 51.2) * mm});
            skPoint(sketch, "E18.3.23", {"position": v(42.4, 42.4) * mm});
            skPoint(sketch, "E18.3.24", {"position": v(9, 52) * mm});
            skPoint(sketch, "E18.3.25", {"position": v(31.8, 52) * mm});
            skLineSegment(sketch, "E18.3.26", {"start": v(0.8, 42.4) * mm, "end": v(8.2, 42.4) * mm});
            skLineSegment(sketch, "E18.3.27", {"start": v(22, 42.4) * mm, "end": v(29.4, 42.4) * mm});
            skLineSegment(sketch, "E18.3.28", {"start": v(32.6, 42.4) * mm, "end": v(40, 42.4) * mm});
            skLineSegment(sketch, "E18.3.29", {"start": v(11.4, 52) * mm, "end": v(18.8, 52) * mm});
            skLineSegment(sketch, "E18.3.30", {"start": v(10.6, 43.2) * mm, "end": v(10.6, 51.2) * mm});
            skPoint(sketch, "E18.3.31", {"position": v(52, 52) * mm});
            skPoint(sketch, "E18.3.32", {"position": v(40.8, 52) * mm});
            skPoint(sketch, "E18.3.33", {"position": v(0, 52) * mm});
            skPoint(sketch, "E18.3.34", {"position": v(30.2, 52) * mm});
            skPoint(sketch, "E18.3.35", {"position": v(21.2, 42.4) * mm});
            skPoint(sketch, "E18.3.36", {"position": v(19.6, 52) * mm});
            skPoint(sketch, "E18.3.37", {"position": v(42.4, 52) * mm});
            skLineSegment(sketch, "E18.3.38", {"start": v(9, 43.2) * mm, "end": v(9, 51.2) * mm});
            skLineSegment(sketch, "E18.3.39", {"start": v(43.2, 42.4) * mm, "end": v(51.2, 42.4) * mm});
            skLineSegment(sketch, "E18.3.40", {"start": v(0.8, 52) * mm, "end": v(8.2, 52) * mm});
            skArc(sketch, "E18.3.41", {"start": v(43.2, 52) * mm, "mid": v(42.63, 51.77) * mm, "end": v(42.4, 51.2) * mm});
            skArc(sketch, "E18.3.42", {"start": v(19.6, 51.2) * mm, "mid": v(19.37, 51.77) * mm, "end": v(18.8, 52) * mm});
            skArc(sketch, "E18.3.43", {"start": v(18.8, 42.4) * mm, "mid": v(19.37, 42.63) * mm, "end": v(19.6, 43.2) * mm});
            skArc(sketch, "E18.3.44", {"start": v(9, 51.2) * mm, "mid": v(8.77, 51.77) * mm, "end": v(8.2, 52) * mm});
            skArc(sketch, "E18.3.45", {"start": v(8.2, 42.4) * mm, "mid": v(8.77, 42.63) * mm, "end": v(9, 43.2) * mm});
            skArc(sketch, "E18.3.46", {"start": v(10.6, 43.2) * mm, "mid": v(10.83, 42.63) * mm, "end": v(11.4, 42.4) * mm});
            skArc(sketch, "E18.3.47", {"start": v(42.4, 43.2) * mm, "mid": v(42.63, 42.63) * mm, "end": v(43.2, 42.4) * mm});
            skArc(sketch, "E18.3.48", {"start": v(40.8, 51.2) * mm, "mid": v(40.57, 51.77) * mm, "end": v(40, 52) * mm});
            skArc(sketch, "E18.3.49", {"start": v(52, 51.2) * mm, "mid": v(51.77, 51.77) * mm, "end": v(51.2, 52) * mm});
            skArc(sketch, "E18.3.50", {"start": v(21.2, 43.2) * mm, "mid": v(21.43, 42.63) * mm, "end": v(22, 42.4) * mm});
            skArc(sketch, "E18.3.51", {"start": v(30.2, 51.2) * mm, "mid": v(29.97, 51.77) * mm, "end": v(29.4, 52) * mm});
            skArc(sketch, "E18.3.52", {"start": v(0.8, 52) * mm, "mid": v(0.23, 51.77) * mm, "end": v(0, 51.2) * mm});
            skArc(sketch, "E18.3.53", {"start": v(11.4, 52) * mm, "mid": v(10.83, 51.77) * mm, "end": v(10.6, 51.2) * mm});
            skArc(sketch, "E18.3.54", {"start": v(29.4, 42.4) * mm, "mid": v(29.97, 42.63) * mm, "end": v(30.2, 43.2) * mm});
            skArc(sketch, "E18.3.55", {"start": v(0, 43.2) * mm, "mid": v(0.23, 42.63) * mm, "end": v(0.8, 42.4) * mm});
            skArc(sketch, "E18.3.56", {"start": v(32.6, 52) * mm, "mid": v(32.03, 51.77) * mm, "end": v(31.8, 51.2) * mm});
            skArc(sketch, "E18.3.57", {"start": v(22, 52) * mm, "mid": v(21.43, 51.77) * mm, "end": v(21.2, 51.2) * mm});
            skArc(sketch, "E18.3.58", {"start": v(51.2, 42.4) * mm, "mid": v(51.77, 42.63) * mm, "end": v(52, 43.2) * mm});
            skArc(sketch, "E18.3.59", {"start": v(31.8, 43.2) * mm, "mid": v(32.03, 42.63) * mm, "end": v(32.6, 42.4) * mm});
            skArc(sketch, "E18.3.60", {"start": v(40, 42.4) * mm, "mid": v(40.57, 42.63) * mm, "end": v(40.8, 43.2) * mm});
            skPoint(sketch, "E18.center", {"position": v(20.4, 20.4) * mm});
            skSolve(sketch);
        }
        {
            var Q0;
            Q0=qSketchRegion(id+"F0",true);
            extrude(context, id + "F1", {"entities" : qUnion([Q0]), "depth" : 0.5 * mm});
        }
    });
